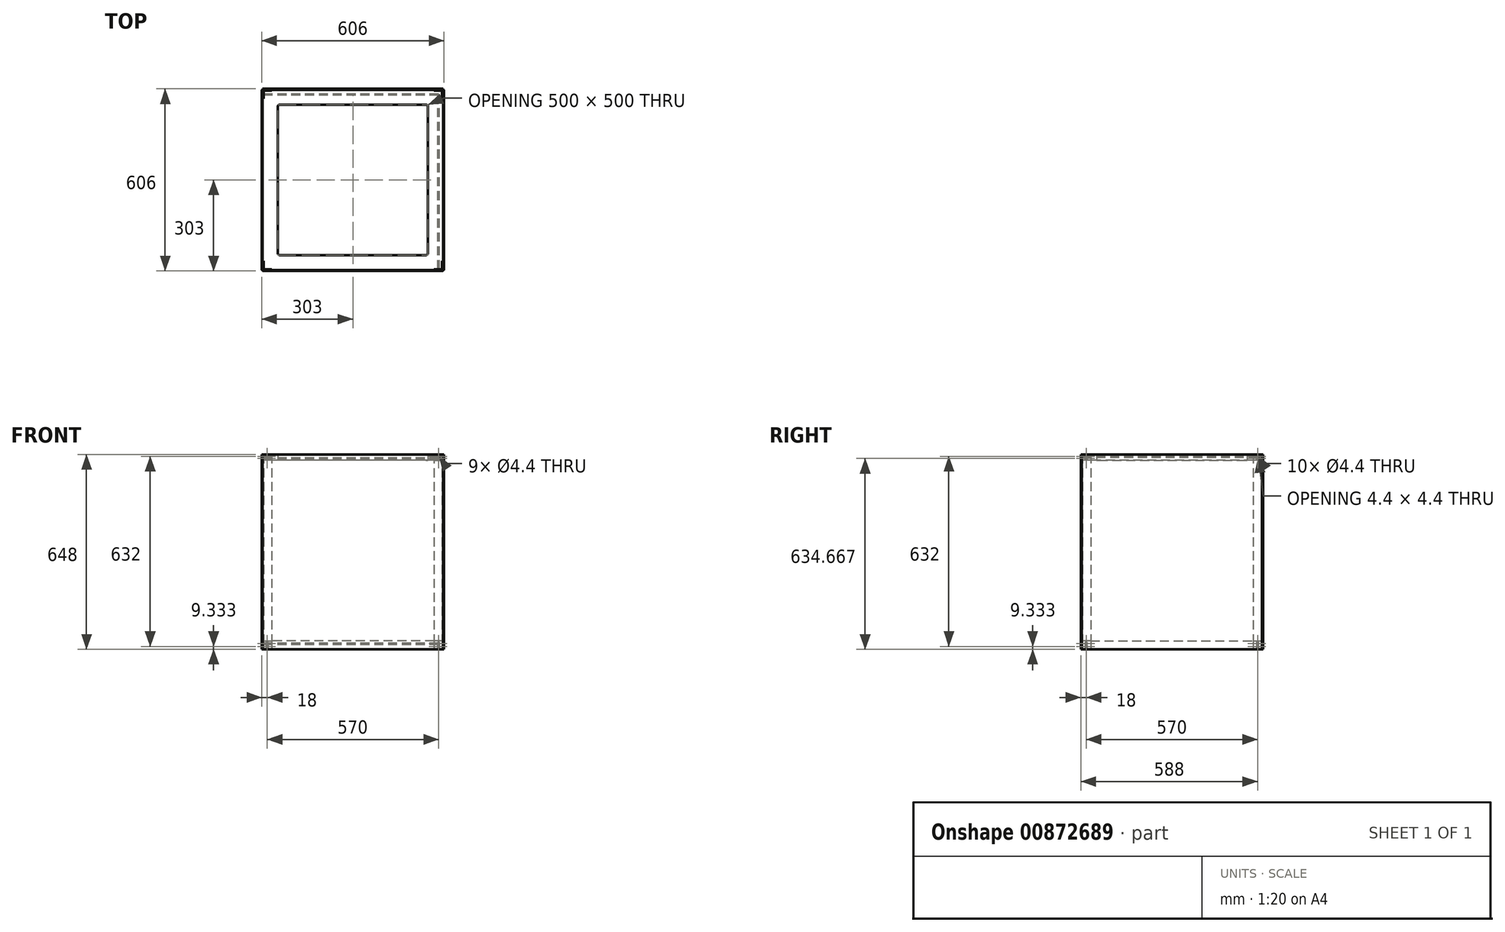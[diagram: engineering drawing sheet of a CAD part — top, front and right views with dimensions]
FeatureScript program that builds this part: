
annotation { "Feature Type Name" : "Feature", "Feature Type Description" : "" }
export const myFeature = defineFeature(function(context is Context, id is Id, definition is map)
    precondition{}
    {
        {
            var Q0;
            Q0=qCreatedBy(makeId("Top.planeOp"),FACE);
            var sketch = newSketch(context, id + "F0", { "sketchPlane" : qUnion([Q0])});
            skLineSegment(sketch, "E0.bottom", {"start": v(300, -300) * mm, "end": v(-300, -300) * mm});
            skLineSegment(sketch, "E0.top", {"start": v(300, 300) * mm, "end": v(-300, 300) * mm});
            skLineSegment(sketch, "E0.left", {"start": v(300, -300) * mm, "end": v(300, 300) * mm});
            skLineSegment(sketch, "E0.right", {"start": v(-300, -300) * mm, "end": v(-300, 300) * mm});
            skPoint(sketch, "E0.middle", {"position": v(0, 0) * mm});
            skLineSegment(sketch, "E1", {"start": v(-300, -270) * mm, "end": v(-297, -270) * mm});
            skLineSegment(sketch, "E2", {"start": v(-297, -270) * mm, "end": v(-297, -297) * mm});
            skLineSegment(sketch, "E3", {"start": v(-297, -297) * mm, "end": v(-270, -297) * mm});
            skLineSegment(sketch, "E4", {"start": v(-270, -297) * mm, "end": v(-270, -300) * mm});
            skLineSegment(sketch, "E5.MirrorCS", {"start": v(270, -297) * mm, "end": v(270, -300) * mm});
            skLineSegment(sketch, "E6.MirrorCS", {"start": v(300, -270) * mm, "end": v(297, -270) * mm});
            skLineSegment(sketch, "E7.MirrorCS", {"start": v(297, -270) * mm, "end": v(297, -297) * mm});
            skLineSegment(sketch, "E8.MirrorCS", {"start": v(297, -297) * mm, "end": v(270, -297) * mm});
            skLineSegment(sketch, "E9.MirrorCS", {"start": v(-297, 270) * mm, "end": v(-297, 297) * mm});
            skLineSegment(sketch, "E10.MirrorCS", {"start": v(-300, 270) * mm, "end": v(-297, 270) * mm});
            skLineSegment(sketch, "E11.MirrorCS", {"start": v(270, 297) * mm, "end": v(270, 300) * mm});
            skLineSegment(sketch, "E12.MirrorCS", {"start": v(297, 297) * mm, "end": v(270, 297) * mm});
            skLineSegment(sketch, "E13.MirrorCS", {"start": v(297, 270) * mm, "end": v(297, 297) * mm});
            skLineSegment(sketch, "E14.MirrorCS", {"start": v(300, 270) * mm, "end": v(297, 270) * mm});
            skLineSegment(sketch, "E15.MirrorCS", {"start": v(-270, 297) * mm, "end": v(-270, 300) * mm});
            skLineSegment(sketch, "E16.MirrorCS", {"start": v(-297, 297) * mm, "end": v(-270, 297) * mm});
            skSolve(sketch);
        }
        {
            var Q0;
            {var subQ6=sQuery(id+"F0.wireOp",EDGE,"E1");Q0=makeQuery(id+"F0.imprint","IMPRINT",FACE,{"disambiguationData":[TD([[makeQuery(id+"F0.imprint","IMPRINT",EDGE,{"derivedFrom":subQ6}),1.0]])]});}
            extrude(context, id + "F1", {"entities" : qUnion([Q0]), "depth" : 28 * mm, "offsetDistance" : 25 * mm});
        }
        {
            var Q0;
            Q0=makeQuery(id+"F1.opExtrude","CAP_FACE",FACE,{"disambiguationData":[OSD([sQuery(id+"F0.wireOp",EDGE,"E0.bottom"),sQuery(id+"F0.wireOp",EDGE,"E0.left"),sQuery(id+"F0.wireOp",EDGE,"E0.right"),sQuery(id+"F0.wireOp",EDGE,"E1"),sQuery(id+"F0.wireOp",EDGE,"E2"),sQuery(id+"F0.wireOp",EDGE,"E3"),sQuery(id+"F0.wireOp",EDGE,"E4"),sQuery(id+"F0.wireOp",EDGE,"E5.MirrorCS"),sQuery(id+"F0.wireOp",EDGE,"E6.MirrorCS"),sQuery(id+"F0.wireOp",EDGE,"E7.MirrorCS"),sQuery(id+"F0.wireOp",EDGE,"E8.MirrorCS"),sQuery(id+"F0.wireOp",EDGE,"E9.MirrorCS"),sQuery(id+"F0.wireOp",EDGE,"E10.MirrorCS"),sQuery(id+"F0.wireOp",EDGE,"E11.MirrorCS"),sQuery(id+"F0.wireOp",EDGE,"E12.MirrorCS"),sQuery(id+"F0.wireOp",EDGE,"E13.MirrorCS"),sQuery(id+"F0.wireOp",EDGE,"E14.MirrorCS"),sQuery(id+"F0.wireOp",EDGE,"E15.MirrorCS"),sQuery(id+"F0.wireOp",EDGE,"E16.MirrorCS"),sQuery(id+"F0.wireOp",EDGE,"E0.top")])],"isStart":false});
            cPlane(context, id + "F2", {"entities" : qUnion([Q0]), "cplaneType" : CPlaneType.OFFSET, "offset" : 600 * mm, "width" : 150 * mm, "height" : 150 * mm});
        }
        {
            var Q0;
            Q0=qCreatedBy(id+"F2.planeOp",FACE);
            var sketch = newSketch(context, id + "F3", { "sketchPlane" : qUnion([Q0])});
            skLineSegment(sketch, "E17.0.0", {"start": v(-270, 300) * mm, "end": v(-270, 297) * mm});
            skLineSegment(sketch, "E17.0.1", {"start": v(-270, 297) * mm, "end": v(-297, 297) * mm});
            skLineSegment(sketch, "E17.0.2", {"start": v(-297, 297) * mm, "end": v(-297, 270) * mm});
            skLineSegment(sketch, "E17.0.3", {"start": v(-297, 270) * mm, "end": v(-300, 270) * mm});
            skLineSegment(sketch, "E17.0.4", {"start": v(-300, 270) * mm, "end": v(-300, -270) * mm});
            skLineSegment(sketch, "E17.0.5", {"start": v(-300, -270) * mm, "end": v(-297, -270) * mm});
            skLineSegment(sketch, "E17.0.6", {"start": v(-297, -270) * mm, "end": v(-297, -297) * mm});
            skLineSegment(sketch, "E17.0.7", {"start": v(-297, -297) * mm, "end": v(-270, -297) * mm});
            skLineSegment(sketch, "E17.0.8", {"start": v(-270, -297) * mm, "end": v(-270, -300) * mm});
            skLineSegment(sketch, "E17.0.9", {"start": v(-270, -300) * mm, "end": v(270, -300) * mm});
            skLineSegment(sketch, "E17.0.10", {"start": v(270, -300) * mm, "end": v(270, -297) * mm});
            skLineSegment(sketch, "E17.0.11", {"start": v(270, -297) * mm, "end": v(297, -297) * mm});
            skLineSegment(sketch, "E17.0.12", {"start": v(297, -297) * mm, "end": v(297, -270) * mm});
            skLineSegment(sketch, "E17.0.13", {"start": v(297, -270) * mm, "end": v(300, -270) * mm});
            skLineSegment(sketch, "E17.0.14", {"start": v(300, -270) * mm, "end": v(300, 270) * mm});
            skLineSegment(sketch, "E17.0.15", {"start": v(300, 270) * mm, "end": v(297, 270) * mm});
            skLineSegment(sketch, "E17.0.16", {"start": v(297, 270) * mm, "end": v(297, 297) * mm});
            skLineSegment(sketch, "E17.0.17", {"start": v(297, 297) * mm, "end": v(270, 297) * mm});
            skLineSegment(sketch, "E17.0.18", {"start": v(270, 297) * mm, "end": v(270, 300) * mm});
            skLineSegment(sketch, "E17.0.19", {"start": v(270, 300) * mm, "end": v(-270, 300) * mm});
            skLineSegment(sketch, "E18.bottom", {"start": v(250, -250) * mm, "end": v(-250, -250) * mm});
            skLineSegment(sketch, "E18.top", {"start": v(250, 250) * mm, "end": v(-250, 250) * mm});
            skLineSegment(sketch, "E18.left", {"start": v(250, -250) * mm, "end": v(250, 250) * mm});
            skLineSegment(sketch, "E18.right", {"start": v(-250, -250) * mm, "end": v(-250, 250) * mm});
            skPoint(sketch, "E18.middle", {"position": v(0, 0) * mm});
            skSolve(sketch);
        }
        {
            var Q0;
            Q0=makeQuery(id+"F3.imprint","IMPRINT",FACE,{"disambiguationData":[TD([[makeQuery(id+"F3.imprint","IMPRINT",EDGE,{"derivedFrom":sQuery(id+"F3.wireOp",EDGE,"E17.0.0")}),1.0]])]});
            extrude(context, id + "F4", {"entities" : qUnion([Q0]), "depth" : 20 * mm, "offsetDistance" : 25 * mm});
        }
        {
            var Q0;
            Q0=makeQuery(id+"F4.opExtrude","SWEPT_EDGE",EDGE,{"disambiguationData":[OSD([sQuery(id+"F3.wireOp",EDGE,"E18.top"),sQuery(id+"F3.wireOp",EDGE,"E18.right")])]});
            var Q1;
            Q1=makeQuery(id+"F4.opExtrude","SWEPT_EDGE",EDGE,{"disambiguationData":[OSD([sQuery(id+"F3.wireOp",EDGE,"E18.top"),sQuery(id+"F3.wireOp",EDGE,"E18.left")])]});
            var Q2;
            Q2=makeQuery(id+"F4.opExtrude","SWEPT_EDGE",EDGE,{"disambiguationData":[OSD([sQuery(id+"F3.wireOp",EDGE,"E18.bottom"),sQuery(id+"F3.wireOp",EDGE,"E18.right")])]});
            var Q3;
            Q3=makeQuery(id+"F4.opExtrude","SWEPT_EDGE",EDGE,{"disambiguationData":[OSD([sQuery(id+"F3.wireOp",EDGE,"E18.bottom"),sQuery(id+"F3.wireOp",EDGE,"E18.left")])]});
            fillet(context, id + "F5", {"entities" : qUnion([Q0, Q1, Q2, Q3]), "radius" : 6.35 * mm, "tangentPropagation" : true, "allowEdgeOverflow" : false});
        }
        {
            var Q0;
            {var subQ0=sQuery(id+"F0.wireOp",EDGE,"E11.MirrorCS");Q0=makeQuery(id+"F0.imprint","IMPRINT",FACE,{"disambiguationData":[TD([[makeQuery(id+"F0.imprint","IMPRINT",EDGE,{"derivedFrom":subQ0}),-1.0]])]});}
            var Q1;
            Q1=makeQuery(id+"F4.opExtrude","CAP_FACE",FACE,{"disambiguationData":[OSD([sQuery(id+"F3.wireOp",EDGE,"E17.0.0"),sQuery(id+"F3.wireOp",EDGE,"E17.0.1"),sQuery(id+"F3.wireOp",EDGE,"E17.0.2"),sQuery(id+"F3.wireOp",EDGE,"E17.0.3"),sQuery(id+"F3.wireOp",EDGE,"E17.0.4"),sQuery(id+"F3.wireOp",EDGE,"E17.0.5"),sQuery(id+"F3.wireOp",EDGE,"E17.0.6"),sQuery(id+"F3.wireOp",EDGE,"E17.0.7"),sQuery(id+"F3.wireOp",EDGE,"E17.0.8"),sQuery(id+"F3.wireOp",EDGE,"E17.0.9"),sQuery(id+"F3.wireOp",EDGE,"E17.0.10"),sQuery(id+"F3.wireOp",EDGE,"E17.0.11"),sQuery(id+"F3.wireOp",EDGE,"E17.0.12"),sQuery(id+"F3.wireOp",EDGE,"E17.0.13"),sQuery(id+"F3.wireOp",EDGE,"E17.0.14"),sQuery(id+"F3.wireOp",EDGE,"E17.0.15"),sQuery(id+"F3.wireOp",EDGE,"E17.0.16"),sQuery(id+"F3.wireOp",EDGE,"E17.0.17"),sQuery(id+"F3.wireOp",EDGE,"E17.0.18"),sQuery(id+"F3.wireOp",EDGE,"E17.0.19"),sQuery(id+"F3.wireOp",EDGE,"E18.bottom"),sQuery(id+"F3.wireOp",EDGE,"E18.top"),sQuery(id+"F3.wireOp",EDGE,"E18.left"),sQuery(id+"F3.wireOp",EDGE,"E18.right")])],"isStart":false});
            extrude(context, id + "F6", {"entities" : qUnion([Q0]), "endBound" : BoundingType.UP_TO_SURFACE, "depth" : 25 * mm, "endBoundEntityFace" : qUnion([Q1]), "offsetDistance" : 25 * mm});
        }
        {
            var Q0;
            Q0=makeQuery(id+"F6.opExtrude","SWEPT_FACE",FACE,{"disambiguationData":[OSD([sQuery(id+"F0.wireOp",EDGE,"E0.top")])]});
            var sketch = newSketch(context, id + "F7", { "sketchPlane" : qUnion([Q0])});
            skLineSegment(sketch, "E19.0", {"start": v(-300, 648) * mm, "end": v(-270, 648) * mm, "construction": true});
            skPoint(sketch, "E20", {"position": v(-285, 641.33) * mm});
            skPoint(sketch, "E20.positionSnap0", {"position": v(-285, 648) * mm});
            skPoint(sketch, "E21.0", {"position": v(-270, 628) * mm});
            skLineSegment(sketch, "E22", {"start": v(-270, 628) * mm, "end": v(-270, 634.67) * mm, "construction": true});
            skLineSegment(sketch, "E23", {"start": v(-270, 634.67) * mm, "end": v(-270, 641.33) * mm, "construction": true});
            skLineSegment(sketch, "E24", {"start": v(-270, 641.33) * mm, "end": v(-270, 648) * mm, "construction": true});
            skPoint(sketch, "E25.0", {"position": v(-270, 0) * mm});
            skPoint(sketch, "E26.0", {"position": v(-270, 28) * mm});
            skLineSegment(sketch, "E27.0", {"start": v(-300, 0) * mm, "end": v(-270, 0) * mm, "construction": true});
            skLineSegment(sketch, "E28", {"start": v(-270, 0) * mm, "end": v(-270, 9.33) * mm, "construction": true});
            skLineSegment(sketch, "E29", {"start": v(-270, 9.33) * mm, "end": v(-270, 18.67) * mm, "construction": true});
            skLineSegment(sketch, "E30", {"start": v(-270, 18.67) * mm, "end": v(-270, 28) * mm, "construction": true});
            skPoint(sketch, "E31", {"position": v(-285, 9.33) * mm});
            skLineSegment(sketch, "E32", {"start": v(-285, 0) * mm, "end": v(-285, 9.33) * mm, "construction": true});
            skSolve(sketch);
        }
        {
            var Q0;
            Q0=sQuery(id+"F7.wireOp",VERTEX,"E20");
            var Q1;
            Q1=sQuery(id+"F7.wireOp",VERTEX,"E31");
            var Q2;
            Q2=makeQuery(id+"F4.opExtrude","SWEPT_BODY",BODY,{"disambiguationData":[OSD([sQuery(id+"F3.wireOp",EDGE,"E17.0.0"),sQuery(id+"F3.wireOp",EDGE,"E17.0.1"),sQuery(id+"F3.wireOp",EDGE,"E17.0.2"),sQuery(id+"F3.wireOp",EDGE,"E17.0.3"),sQuery(id+"F3.wireOp",EDGE,"E17.0.4"),sQuery(id+"F3.wireOp",EDGE,"E17.0.5"),sQuery(id+"F3.wireOp",EDGE,"E17.0.6"),sQuery(id+"F3.wireOp",EDGE,"E17.0.7"),sQuery(id+"F3.wireOp",EDGE,"E17.0.8"),sQuery(id+"F3.wireOp",EDGE,"E17.0.9"),sQuery(id+"F3.wireOp",EDGE,"E17.0.10"),sQuery(id+"F3.wireOp",EDGE,"E17.0.11"),sQuery(id+"F3.wireOp",EDGE,"E17.0.12"),sQuery(id+"F3.wireOp",EDGE,"E17.0.13"),sQuery(id+"F3.wireOp",EDGE,"E17.0.14"),sQuery(id+"F3.wireOp",EDGE,"E17.0.15"),sQuery(id+"F3.wireOp",EDGE,"E17.0.16"),sQuery(id+"F3.wireOp",EDGE,"E17.0.17"),sQuery(id+"F3.wireOp",EDGE,"E17.0.18"),sQuery(id+"F3.wireOp",EDGE,"E17.0.19"),sQuery(id+"F3.wireOp",EDGE,"E18.bottom"),sQuery(id+"F3.wireOp",EDGE,"E18.top"),sQuery(id+"F3.wireOp",EDGE,"E18.left"),sQuery(id+"F3.wireOp",EDGE,"E18.right")])]});
            var Q3;
            Q3=makeQuery(id+"F6.opExtrude","SWEPT_BODY",BODY,{"disambiguationData":[OSD([sQuery(id+"F0.wireOp",EDGE,"E0.left"),sQuery(id+"F0.wireOp",EDGE,"E11.MirrorCS"),sQuery(id+"F0.wireOp",EDGE,"E12.MirrorCS"),sQuery(id+"F0.wireOp",EDGE,"E13.MirrorCS"),sQuery(id+"F0.wireOp",EDGE,"E14.MirrorCS"),sQuery(id+"F0.wireOp",EDGE,"E0.top")])]});
            hole(context, id + "F8", {"style" : HoleStyle.C_SINK, "endStyle" : HoleEndStyle.THROUGH, "standardTappedOrClearance" : lookupTablePath({ "fit" : "Normal", "standard" : "ISO", "size" : "M4", "type" : "Clearance" }), "standardBlindInLast" : lookupTablePath({ "fit" : "Standard", "standard" : "ISO", "size" : "M4", "type" : "Clearance" }), "holeDiameter" : 4.4 * mm, "cSinkDiameter" : 8.96 * mm, "cSinkAngle" : 90 * degree, "majorDiameter" : 5 * mm, "isTappedThrough" : true, "tappedDepth" : 12 * mm, "tapClearance" : 3, "locations" : qUnion([Q0, Q1]), "scope" : qUnion([Q2, Q3])});
        }
        {
            var Q0;
            Q0=makeQuery(id+"F6.opExtrude","SWEPT_FACE",FACE,{"disambiguationData":[OSD([sQuery(id+"F0.wireOp",EDGE,"E0.left")])]});
            var sketch = newSketch(context, id + "F9", { "sketchPlane" : qUnion([Q0])});
            skPoint(sketch, "E33.0", {"position": v(300, 634.67) * mm});
            skPoint(sketch, "E34.0", {"position": v(285, 648) * mm});
            skPoint(sketch, "E35", {"position": v(285, 634.67) * mm});
            skPoint(sketch, "E36.0", {"position": v(300, 18.67) * mm});
            skPoint(sketch, "E37.0", {"position": v(285, 0) * mm});
            skPoint(sketch, "E38", {"position": v(285, 18.67) * mm});
            skSolve(sketch);
        }
        {
            var Q0;
            Q0=sQuery(id+"F9.wireOp",VERTEX,"E38");
            var Q1;
            Q1=sQuery(id+"F9.wireOp",VERTEX,"E35");
            var Q2;
            Q2=makeQuery(id+"F4.opExtrude","SWEPT_BODY",BODY,{"disambiguationData":[OSD([sQuery(id+"F3.wireOp",EDGE,"E17.0.0"),sQuery(id+"F3.wireOp",EDGE,"E17.0.1"),sQuery(id+"F3.wireOp",EDGE,"E17.0.2"),sQuery(id+"F3.wireOp",EDGE,"E17.0.3"),sQuery(id+"F3.wireOp",EDGE,"E17.0.4"),sQuery(id+"F3.wireOp",EDGE,"E17.0.5"),sQuery(id+"F3.wireOp",EDGE,"E17.0.6"),sQuery(id+"F3.wireOp",EDGE,"E17.0.7"),sQuery(id+"F3.wireOp",EDGE,"E17.0.8"),sQuery(id+"F3.wireOp",EDGE,"E17.0.9"),sQuery(id+"F3.wireOp",EDGE,"E17.0.10"),sQuery(id+"F3.wireOp",EDGE,"E17.0.11"),sQuery(id+"F3.wireOp",EDGE,"E17.0.12"),sQuery(id+"F3.wireOp",EDGE,"E17.0.13"),sQuery(id+"F3.wireOp",EDGE,"E17.0.14"),sQuery(id+"F3.wireOp",EDGE,"E17.0.15"),sQuery(id+"F3.wireOp",EDGE,"E17.0.16"),sQuery(id+"F3.wireOp",EDGE,"E17.0.17"),sQuery(id+"F3.wireOp",EDGE,"E17.0.18"),sQuery(id+"F3.wireOp",EDGE,"E17.0.19"),sQuery(id+"F3.wireOp",EDGE,"E18.bottom"),sQuery(id+"F3.wireOp",EDGE,"E18.top"),sQuery(id+"F3.wireOp",EDGE,"E18.left"),sQuery(id+"F3.wireOp",EDGE,"E18.right")])]});
            var Q3;
            Q3=makeQuery(id+"F6.opExtrude","SWEPT_BODY",BODY,{"disambiguationData":[OSD([sQuery(id+"F0.wireOp",EDGE,"E0.left"),sQuery(id+"F0.wireOp",EDGE,"E11.MirrorCS"),sQuery(id+"F0.wireOp",EDGE,"E12.MirrorCS"),sQuery(id+"F0.wireOp",EDGE,"E13.MirrorCS"),sQuery(id+"F0.wireOp",EDGE,"E14.MirrorCS"),sQuery(id+"F0.wireOp",EDGE,"E0.top")])]});
            var Q4;
            Q4=makeQuery(id+"F1.opExtrude","SWEPT_BODY",BODY,{"disambiguationData":[OSD([sQuery(id+"F0.wireOp",EDGE,"E0.bottom"),sQuery(id+"F0.wireOp",EDGE,"E0.left"),sQuery(id+"F0.wireOp",EDGE,"E0.right"),sQuery(id+"F0.wireOp",EDGE,"E1"),sQuery(id+"F0.wireOp",EDGE,"E2"),sQuery(id+"F0.wireOp",EDGE,"E3"),sQuery(id+"F0.wireOp",EDGE,"E4"),sQuery(id+"F0.wireOp",EDGE,"E5.MirrorCS"),sQuery(id+"F0.wireOp",EDGE,"E6.MirrorCS"),sQuery(id+"F0.wireOp",EDGE,"E7.MirrorCS"),sQuery(id+"F0.wireOp",EDGE,"E8.MirrorCS"),sQuery(id+"F0.wireOp",EDGE,"E9.MirrorCS"),sQuery(id+"F0.wireOp",EDGE,"E10.MirrorCS"),sQuery(id+"F0.wireOp",EDGE,"E11.MirrorCS"),sQuery(id+"F0.wireOp",EDGE,"E12.MirrorCS"),sQuery(id+"F0.wireOp",EDGE,"E13.MirrorCS"),sQuery(id+"F0.wireOp",EDGE,"E14.MirrorCS"),sQuery(id+"F0.wireOp",EDGE,"E15.MirrorCS"),sQuery(id+"F0.wireOp",EDGE,"E16.MirrorCS"),sQuery(id+"F0.wireOp",EDGE,"E0.top")])]});
            hole(context, id + "F10", {"style" : HoleStyle.C_SINK, "endStyle" : HoleEndStyle.THROUGH, "standardTappedOrClearance" : lookupTablePath({ "fit" : "Normal", "standard" : "ISO", "size" : "M4", "type" : "Clearance" }), "standardBlindInLast" : lookupTablePath({ "fit" : "Standard", "standard" : "ISO", "size" : "M4", "type" : "Clearance" }), "holeDiameter" : 4.4 * mm, "cSinkDiameter" : 8.96 * mm, "cSinkAngle" : 90 * degree, "majorDiameter" : 5 * mm, "isTappedThrough" : true, "tappedDepth" : 12 * mm, "tapClearance" : 3, "locations" : qUnion([Q0, Q1]), "scope" : qUnion([Q2, Q3, Q4])});
        }
        {
            var Q0;
            Q0=qCreatedBy(makeId("Front.planeOp"),FACE);
            var sketch = newSketch(context, id + "F11", { "sketchPlane" : qUnion([Q0])});
            skLineSegment(sketch, "E39", {"start": v(0, 0) * mm, "end": v(0, 275.16) * mm});
            skSolve(sketch);
        }
        {
            var Q0;
            {var subQ0=sQuery(id+"F0.wireOp",EDGE,"E0.top");Q0=makeQuery(id+"F7.imprint","IMPRINT",FACE,{"disambiguationData":[TD([[makeQuery(id+"F7.imprint","IMPRINT",EDGE,{"derivedFrom":makeQuery(id+"F6.opExtrude","CAP_EDGE",EDGE,{"disambiguationData":[OSD([subQ0])],"isStart":true})}),1.0]])]});}
            var sketch = newSketch(context, id + "F12", { "sketchPlane" : qUnion([Q0])});
            skLineSegment(sketch, "E40.0", {"start": v(-300, 648) * mm, "end": v(-300, 0) * mm});
            skPoint(sketch, "E41.0", {"position": v(300, 648) * mm});
            skLineSegment(sketch, "E42.bottom", {"start": v(-300, 0) * mm, "end": v(300, 0) * mm});
            skLineSegment(sketch, "E42.top", {"start": v(-300, 648) * mm, "end": v(300, 648) * mm});
            skLineSegment(sketch, "E42.left", {"start": v(-300, 0) * mm, "end": v(-300, 648) * mm});
            skLineSegment(sketch, "E42.right", {"start": v(300, 0) * mm, "end": v(300, 648) * mm});
            skSolve(sketch);
        }
        {
            var Q0;
            Q0 = qSketchRegion(id + "F12", true);
            extrude(context, id + "F13", {"entities" : qUnion([Q0]), "depth" : 3 * mm, "offsetDistance" : 25 * mm});
        }
        {
            var Q0;
            Q0=makeQuery(id+"F6.opExtrude","SWEPT_BODY",BODY,{"disambiguationData":[OSD([sQuery(id+"F0.wireOp",EDGE,"E0.left"),sQuery(id+"F0.wireOp",EDGE,"E11.MirrorCS"),sQuery(id+"F0.wireOp",EDGE,"E12.MirrorCS"),sQuery(id+"F0.wireOp",EDGE,"E13.MirrorCS"),sQuery(id+"F0.wireOp",EDGE,"E14.MirrorCS"),sQuery(id+"F0.wireOp",EDGE,"E0.top")])]});
            var Q1;
            Q1=makeQuery(id+"F13.opExtrude","SWEPT_BODY",BODY,{"disambiguationData":[OSD([sQuery(id+"F12.wireOp",EDGE,"E42.bottom"),sQuery(id+"F12.wireOp",EDGE,"E42.top"),sQuery(id+"F12.wireOp",EDGE,"E42.left"),sQuery(id+"F12.wireOp",EDGE,"E42.right")])]});
            var Q2;
            Q2=sQuery(id+"F11.wireOp",EDGE,"E39");
            circularPattern(context, id + "F14", {"entities" : qUnion([Q0, Q1]), "axis" : qUnion([Q2]), "angle" : 360 * degree, "instanceCount" : 4, "equalSpace" : true});
        }
    });
